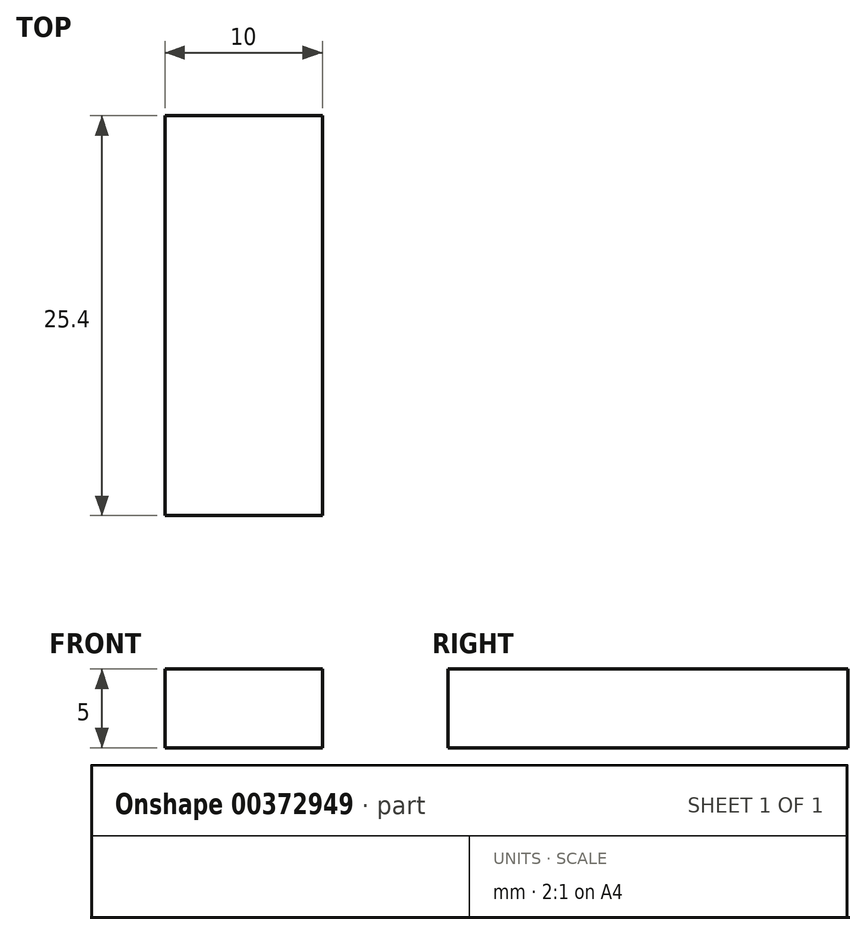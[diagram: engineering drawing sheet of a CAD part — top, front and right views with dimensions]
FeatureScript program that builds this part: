
annotation { "Feature Type Name" : "Feature", "Feature Type Description" : "" }
export const myFeature = defineFeature(function(context is Context, id is Id, definition is map)
    precondition{}
    {
        {
            var Q0;
            Q0=qCreatedBy(makeId("Front.planeOp"),FACE);
            var sketch = newSketch(context, id + "F0", { "sketchPlane" : qUnion([Q0])});
            skLineSegment(sketch, "E0.bottom", {"start": v(0, 0) * mm, "end": v(10, 0) * mm});
            skLineSegment(sketch, "E0.top", {"start": v(0, 5) * mm, "end": v(10, 5) * mm});
            skLineSegment(sketch, "E0.left", {"start": v(0, 0) * mm, "end": v(0, 5) * mm});
            skLineSegment(sketch, "E0.right", {"start": v(10, 0) * mm, "end": v(10, 5) * mm});
            skSolve(sketch);
        }
        {
            var Q0;
            Q0 = qSketchRegion(id + "F0", true);
            extrude(context, id + "F1", {"entities" : qUnion([Q0]), "depth" : 25.4 * mm});
        }
    });
